# Revit family: Gira_597900
name_source: partatom
category: Elektroinstallationen
revit_build: Autodesk Revit 2017 (Build: 20160225_1515(x64)
units: mm (PartAtom-declared; Revit-internal decimal feet)

## family parameters
Basisbauteil = Fläche
Beim Laden mit Abzugskörper schneiden = Nein
Bemaßung runder Anschluss = Durchmesser verwenden
Beschriftungsausrichtung beibehalten = Nein
Gemeinsam genutzt = Nein
Raumberechnungspunkt = Nein
Teiletyp = Normal

## types (1)
- I/O-Modul Stationsbus AP 8/8 REG Rufsystem 834 Plus
    Anzahl der binären Eingänge = 0
    Art der Spannungsversorgung = extern
    Ausführung Text = sonstige
    BIM = https://media.stage.bim.site 8f.rfa
    BIMSITE_PRODUCT_ID = ebd165a750fd671c72032433e5bbcc74c6ab6b62
    Beschreibung = I O-Modul Stationsbus AP 8 Eingänge 8 Ausgänge  REG Die Eingänge der I O-Module dienen zur Einbindung von Fremdanlagen und technischen Alarmmeldungen (z. B. BMA, Aufzugalarm, Sicherheitsbeleuchtung, andere Lichtrufsysteme, Hausklingel etc.). Die Ausgänge dienen zum Schalten externer Geräte wie Lampen, andere Lichtrufsysteme, Türmagneten, Hupen usw.  Merkmale: Eingänge:  Die Eingänge sind galvanisch getrennt und können getrennt mit unterschiedlichen Bezugspotenzialen arbeiten.  Die Koppeleinheit ist für die Eingänge im Bereich AC DC 5-30 V ausgelegt.  Die Koppeleinheit ist selbstüberwachend. Ausgänge:  Die Ausgänge sind einzeln konfigurierbar.  Die Ansteuerung der Ausgänge erfolgt über entsprechende Software gemäß Konfiguration.  Jedes Ausgangsrelais ist potenzialfrei als Umschaltekontakt nutzbar und bis 8 A belastbar.  Das I O-Modul Stationsbus AP (REG) verfügt über acht Eingänge und acht Ausgänge.
    Breite in Teilungseinheiten = 0
    Busfähig = 2-Draht
    Bussystem Funkbus = Nein
    Bussystem KNX = Nein
    Bussystem KNX-Funk = Nein
    Bussystem LON = Nein
    Bussystem Powernet = Nein
    Datenblatt = https://media.stage.bim.site
    Datenblatt 1 = https://media.stage.bim.site
    GTIN = 4010337105442
    Geeignet für C-Last = Nein
    HAN = 597900
    HeinzeBIM = https://www.heinze.de
    Hersteller = Gira
    Kosten = 0 $
    Max. Anzahl der Schaltausgänge = 0
    Mit Busankopplung = Nein
    Mit LED-Anzeige = Nein
    Produktseite = https://media.stage.bim.site
    Typname = I/O-Modul Stationsbus AP 8/8 REG Rufsystem 834 Plus
    URL = https://www.gira.de
    Vor Ort-/Handbedienung = Nein
    Vorgabe-Ansicht = 1219 mm
    Zusammenstellung = Basiselement

## geometry (parser evidence)
native form markers: Sweep x2
no freeform markers — native parametric forms only
